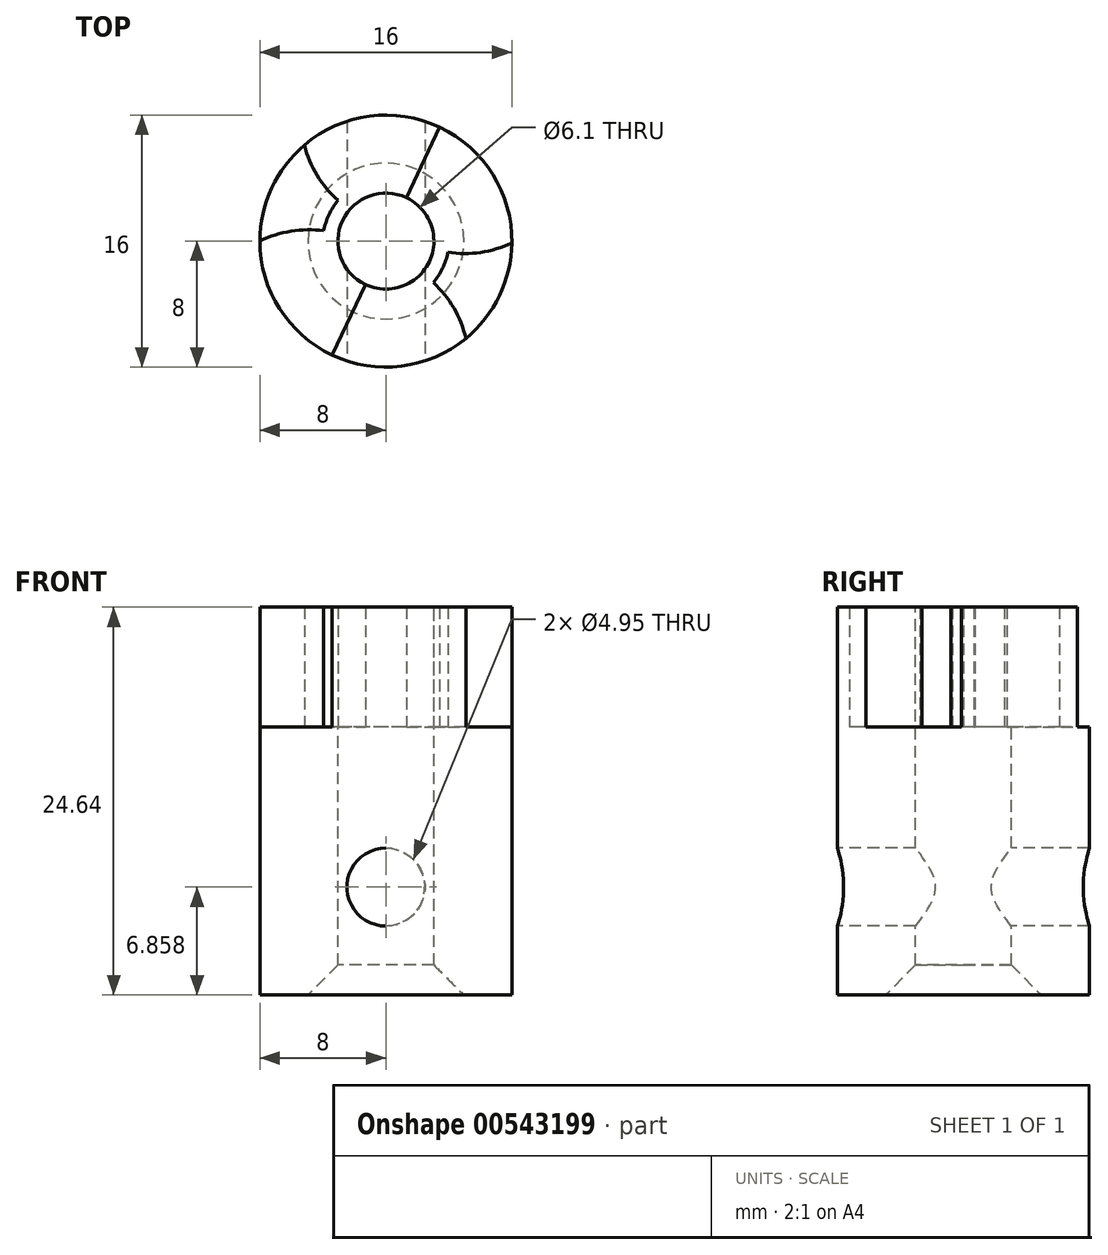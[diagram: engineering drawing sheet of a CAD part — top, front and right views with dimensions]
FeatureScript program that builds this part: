
annotation { "Feature Type Name" : "Feature", "Feature Type Description" : "" }
export const myFeature = defineFeature(function(context is Context, id is Id, definition is map)
    precondition{}
    {
        {
            var Q0;
            Q0=qCreatedBy(makeId("Top.planeOp"),FACE);
            var sketch = newSketch(context, id + "F0", { "sketchPlane" : qUnion([Q0])});
            skCircle(sketch, "E0", {"center": v(0, 0) * mm, "radius": 3.05 * mm});
            skCircle(sketch, "E1", {"center": v(0, 0) * mm, "radius": 8 * mm});
            skSolve(sketch);
        }
        {
            var Q0;
            Q0=makeQuery(id+"F0.imprint","IMPRINT",FACE,{"disambiguationData":[TD([[makeQuery(id+"F0.imprint","IMPRINT",EDGE,{"derivedFrom":sQuery(id+"F0.wireOp",EDGE,"E0")}),-1.0]])]});
            extrude(context, id + "F1", {"entities" : qUnion([Q0]), "depth" : 17.02 * mm, "offsetDistance" : 25.4 * mm});
        }
        {
            var Q0;
            Q0=makeQuery(id+"F1.opExtrude","CAP_FACE",FACE,{"disambiguationData":[OSD([sQuery(id+"F0.wireOp",EDGE,"E0"),sQuery(id+"F0.wireOp",EDGE,"E1")])],"isStart":false});
            var sketch = newSketch(context, id + "F2", { "sketchPlane" : qUnion([Q0])});
            skSolve(sketch);
        }
        {
            var Q0;
            Q0=qCreatedBy(makeId("Top.planeOp"),FACE);
            var sketch = newSketch(context, id + "F3", { "sketchPlane" : qUnion([Q0])});
            skLineSegment(sketch, "E2.bottom", {"start": v(8, 8) * mm, "end": v(-8, 8) * mm});
            skLineSegment(sketch, "E2.top", {"start": v(8, -8) * mm, "end": v(-8, -8) * mm});
            skLineSegment(sketch, "E2.left", {"start": v(8, 8) * mm, "end": v(8, -8) * mm});
            skLineSegment(sketch, "E2.right", {"start": v(-8, 8) * mm, "end": v(-8, -8) * mm});
            skPoint(sketch, "E2.middle", {"position": v(0, 0) * mm});
            skSolve(sketch);
        }
        {
            var Q0;
            Q0=makeQuery(id+"F3.imprint","IMPRINT",FACE,{"disambiguationData":[TD([[makeQuery(id+"F3.imprint","IMPRINT",EDGE,{"derivedFrom":sQuery(id+"F3.wireOp",EDGE,"E2.bottom")}),1.0]])]});
            extrude(context, id + "F4", {"entities" : qUnion([Q0]), "operationType" : NewBodyOperationType.ADD, "depth" : 17.02 * mm, "offsetDistance" : 25.4 * mm});
        }
        {
            var Q0;
            Q0=makeQuery(id+"F4.opExtrude","SWEPT_FACE",FACE,{"disambiguationData":[OSD([sQuery(id+"F3.wireOp",EDGE,"E2.top")])]});
            var sketch = newSketch(context, id + "F5", { "sketchPlane" : qUnion([Q0])});
            skCircle(sketch, "E3", {"center": v(0, 6.86) * mm, "radius": 2.48 * mm});
            skPoint(sketch, "E3.centerSnap0", {"position": v(0, 0) * mm});
            skSolve(sketch);
        }
        {
            var Q0;
            Q0=makeQuery(id+"F5.imprint","IMPRINT",FACE,{"disambiguationData":[TD([[makeQuery(id+"F5.imprint","IMPRINT",EDGE,{"derivedFrom":sQuery(id+"F5.wireOp",EDGE,"E3")}),1.0]])]});
            extrude(context, id + "F6", {"entities" : qUnion([Q0]), "operationType" : NewBodyOperationType.REMOVE, "oppositeDirection" : true, "depth" : 25.4 * mm, "offsetDistance" : 25.4 * mm});
        }
        {
            var Q0;
            Q0=makeQuery(id+"F4.opExtrude","SWEPT_EDGE",EDGE,{"disambiguationData":[OSD([sQuery(id+"F3.wireOp",EDGE,"E2.top"),sQuery(id+"F3.wireOp",EDGE,"E2.left")])]});
            var Q1;
            Q1=makeQuery(id+"F4.opExtrude","SWEPT_EDGE",EDGE,{"disambiguationData":[OSD([sQuery(id+"F3.wireOp",EDGE,"E2.bottom"),sQuery(id+"F3.wireOp",EDGE,"E2.left")])]});
            var Q2;
            Q2=makeQuery(id+"F4.opExtrude","SWEPT_EDGE",EDGE,{"disambiguationData":[OSD([sQuery(id+"F3.wireOp",EDGE,"E2.top"),sQuery(id+"F3.wireOp",EDGE,"E2.right")])]});
            var Q3;
            Q3=makeQuery(id+"F4.opExtrude","SWEPT_EDGE",EDGE,{"disambiguationData":[OSD([sQuery(id+"F3.wireOp",EDGE,"E2.bottom"),sQuery(id+"F3.wireOp",EDGE,"E2.right")])]});
            fillet(context, id + "F7", {"entities" : qUnion([Q0, Q1, Q2, Q3]), "radius" : 8 * mm, "tangentPropagation" : true, "allowEdgeOverflow" : false});
        }
        {
            var Q0;
            Q0=makeQuery(id+"F2.imprint","IMPRINT",FACE,{"disambiguationData":[TD([[makeQuery(id+"F2.imprint","IMPRINT",EDGE,{"derivedFrom":makeQuery(id+"F1.opExtrude","CAP_EDGE",EDGE,{"disambiguationData":[OSD([sQuery(id+"F0.wireOp",EDGE,"E0")])],"isStart":false})}),1.0]])]});
            extrude(context, id + "F8", {"entities" : qUnion([Q0]), "operationType" : NewBodyOperationType.REMOVE, "oppositeDirection" : true, "depth" : 25.4 * mm, "offsetDistance" : 25.4 * mm});
        }
        {
            var Q0;
            Q0=makeQuery(id+"F4.boolean.opBoolean","MERGE",FACE,{"derivedFrom":[makeQuery(id+"F1.opExtrude","CAP_FACE",FACE,{"disambiguationData":[OSD([sQuery(id+"F0.wireOp",EDGE,"E0"),sQuery(id+"F0.wireOp",EDGE,"E1")])],"isStart":false}),makeQuery(id+"F4.opExtrude","CAP_FACE",FACE,{"disambiguationData":[OSD([sQuery(id+"F3.wireOp",EDGE,"E2.bottom"),sQuery(id+"F3.wireOp",EDGE,"E2.top"),sQuery(id+"F3.wireOp",EDGE,"E2.left"),sQuery(id+"F3.wireOp",EDGE,"E2.right")])],"isStart":false})]});
            var sketch = newSketch(context, id + "F9", { "sketchPlane" : qUnion([Q0])});
            skArc(sketch, "E4", {"start": v(-5.17, 6.1) * mm, "mid": v(-7.26, 3.37) * mm, "end": v(-8, 0) * mm});
            skArc(sketch, "E5", {"start": v(-3.05, 2.59) * mm, "mid": v(-3.62, 1.68) * mm, "end": v(-3.95, 0.65) * mm});
            skArc(sketch, "E6", {"start": v(-3.95, 0.65) * mm, "mid": v(-6.02, 0.63) * mm, "end": v(-8, 0) * mm});
            skArc(sketch, "E7", {"start": v(-5.17, 6.1) * mm, "mid": v(-4.37, 4.19) * mm, "end": v(-3.05, 2.59) * mm});
            skLineSegment(sketch, "E8", {"start": v(0, 0) * mm, "end": v(3.91, 8.3) * mm});
            skLineSegment(sketch, "E9", {"start": v(3.91, 8.3) * mm, "end": v(-3.42, -7.24) * mm});
            skArc(sketch, "E10.MirrorCS", {"start": v(3.94, -0.7) * mm, "mid": v(3.6, -1.73) * mm, "end": v(3.01, -2.63) * mm});
            skArc(sketch, "E11.MirrorCS", {"start": v(8, -0.11) * mm, "mid": v(6.01, -0.72) * mm, "end": v(3.94, -0.7) * mm});
            skArc(sketch, "E12.MirrorCS", {"start": v(3.01, -2.63) * mm, "mid": v(4.31, -4.25) * mm, "end": v(5.08, -6.18) * mm});
            skArc(sketch, "E13.MirrorCS", {"start": v(8, -0.11) * mm, "mid": v(7.21, -3.47) * mm, "end": v(5.08, -6.18) * mm});
            skSolve(sketch);
        }
        {
            var Q0;
            Q0=makeQuery(id+"F9.imprint","IMPRINT",FACE,{"disambiguationData":[TD([[makeQuery(id+"F9.imprint","IMPRINT",EDGE,{"derivedFrom":sQuery(id+"F9.wireOp",EDGE,"E4")}),1.0]])]});
            var Q1;
            {var subQ0=sQuery(id+"F9.wireOp",EDGE,"E11.MirrorCS");Q1=makeQuery(id+"F9.imprint","IMPRINT",FACE,{"disambiguationData":[TD([[makeQuery(id+"F9.imprint","IMPRINT",EDGE,{"derivedFrom":subQ0}),1.0]])]});}
            extrude(context, id + "F10", {"entities" : qUnion([Q0, Q1]), "operationType" : NewBodyOperationType.ADD, "depth" : 7.62 * mm, "offsetDistance" : 25.4 * mm});
        }
        {
            var Q0;
            {var subQ0=sQuery(id+"F0.wireOp",EDGE,"E0");Q0=makeQuery(id+"F8.boolean.opBoolean","INTERSECT",EDGE,{"derivedFrom":[makeQuery(id+"F4.boolean.opBoolean","MERGE",FACE,{"derivedFrom":[makeQuery(id+"F1.opExtrude","CAP_FACE",FACE,{"disambiguationData":[OSD([subQ0,sQuery(id+"F0.wireOp",EDGE,"E1")])],"isStart":true}),makeQuery(id+"F4.opExtrude","CAP_FACE",FACE,{"disambiguationData":[OSD([sQuery(id+"F3.wireOp",EDGE,"E2.bottom"),sQuery(id+"F3.wireOp",EDGE,"E2.top"),sQuery(id+"F3.wireOp",EDGE,"E2.left"),sQuery(id+"F3.wireOp",EDGE,"E2.right")])],"isStart":true})]}),makeQuery(id+"F8.opExtrude","SWEPT_FACE",FACE,{"disambiguationData":[OSD([subQ0])]})]});}
            chamfer(context, id + "F11", {"entities" : qUnion([Q0]), "width" : 1.9 * mm, "tangentPropagation" : true});
        }
    });
